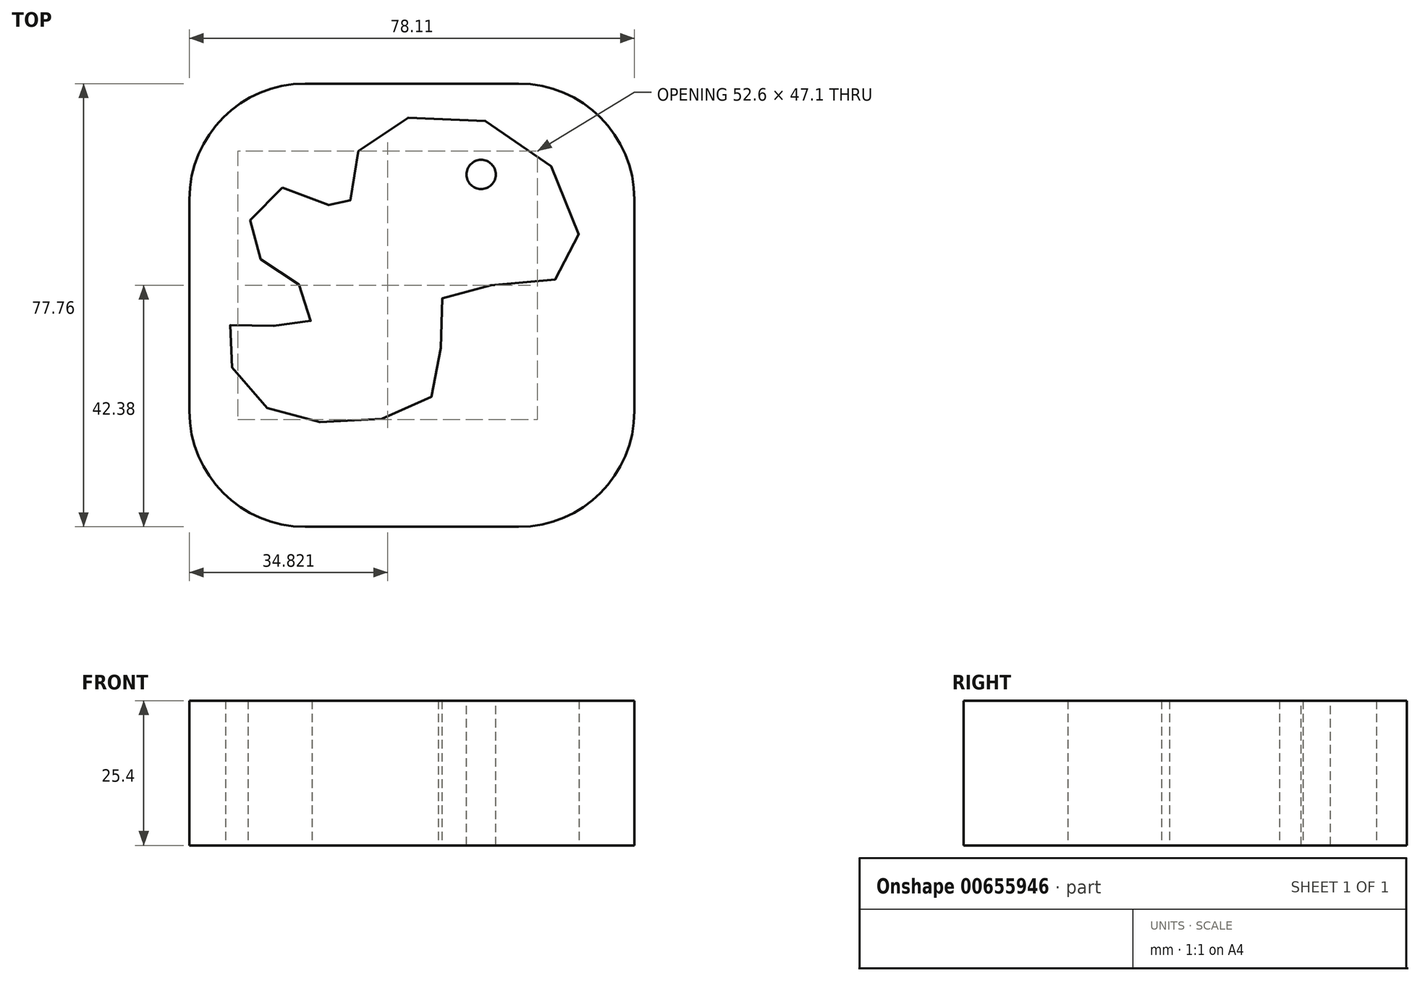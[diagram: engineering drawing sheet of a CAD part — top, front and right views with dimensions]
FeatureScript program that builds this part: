
annotation { "Feature Type Name" : "Feature", "Feature Type Description" : "" }
export const myFeature = defineFeature(function(context is Context, id is Id, definition is map)
    precondition{}
    {
        {
            var Q0;
            Q0=qCreatedBy(makeId("Top.planeOp"),FACE);
            var sketch = newSketch(context, id + "F0", { "sketchPlane" : qUnion([Q0])});
            skLineSegment(sketch, "E0.bottom", {"start": v(-136.12, 47) * mm, "end": v(-58, 47) * mm});
            skLineSegment(sketch, "E0.top", {"start": v(-136.12, -30.76) * mm, "end": v(-58, -30.76) * mm});
            skLineSegment(sketch, "E0.left", {"start": v(-136.12, 47) * mm, "end": v(-136.12, -30.76) * mm});
            skLineSegment(sketch, "E0.right", {"start": v(-58, 47) * mm, "end": v(-58, -30.76) * mm});
            skSolve(sketch);
        }
        {
            var Q0;
            Q0=makeQuery(id+"F0.imprint","IMPRINT",FACE,{"disambiguationData":[TD([[makeQuery(id+"F0.imprint","IMPRINT",EDGE,{"derivedFrom":sQuery(id+"F0.wireOp",EDGE,"E0.bottom")}),-1.0]])]});
            extrude(context, id + "F1", {"entities" : qUnion([Q0]), "depth" : 25.4 * mm, "offsetDistance" : 25.4 * mm});
        }
        {
            var Q0;
            Q0=makeQuery(id+"F1.opExtrude","CAP_FACE",FACE,{"disambiguationData":[OSD([sQuery(id+"F0.wireOp",EDGE,"E0.bottom"),sQuery(id+"F0.wireOp",EDGE,"E0.top"),sQuery(id+"F0.wireOp",EDGE,"E0.left"),sQuery(id+"F0.wireOp",EDGE,"E0.right")])],"isStart":false});
            var sketch = newSketch(context, id + "F2", { "sketchPlane" : qUnion([Q0])});
            skFitSpline(sketch, "E1", {"points": [v(-119.78, 28.73) * mm, v(-125.58, 18.83) * mm, v(-116.26, 11.07) * mm, v(-115.93, 4.23) * mm, v(-128.51, 4.94) * mm, v(-126.17, -6.83) * mm, v(-108.66, -12.45) * mm, v(-92.21, -5.58) * mm, v(-91.18, 10) * mm, v(-70.08, 13.7) * mm, v(-77.51, 37.26) * mm, v(-106, 35.99) * mm, v(-108.7, 24.71) * mm, v(-119.78, 28.73) * mm]});
            skCircle(sketch, "E2", {"center": v(-84.92, 31.06) * mm, "radius": 2.57 * mm});
            skSolve(sketch);
        }
        {
            var Q0;
            Q0 = qSketchRegion(id + "F2", true);
            extrude(context, id + "F3", {"entities" : qUnion([Q0]), "operationType" : NewBodyOperationType.REMOVE, "endBound" : BoundingType.THROUGH_ALL, "oppositeDirection" : true, "depth" : 25.4 * mm, "offsetDistance" : 25.4 * mm});
        }
        {
            var Q0;
            Q0=makeQuery(id+"F1.opExtrude","SWEPT_EDGE",EDGE,{"disambiguationData":[OSD([sQuery(id+"F0.wireOp",EDGE,"E0.top"),sQuery(id+"F0.wireOp",EDGE,"E0.right")])]});
            var Q1;
            Q1=makeQuery(id+"F1.opExtrude","SWEPT_EDGE",EDGE,{"disambiguationData":[OSD([sQuery(id+"F0.wireOp",EDGE,"E0.top"),sQuery(id+"F0.wireOp",EDGE,"E0.left")])]});
            var Q2;
            Q2=makeQuery(id+"F1.opExtrude","SWEPT_EDGE",EDGE,{"disambiguationData":[OSD([sQuery(id+"F0.wireOp",EDGE,"E0.bottom"),sQuery(id+"F0.wireOp",EDGE,"E0.right")])]});
            var Q3;
            Q3=makeQuery(id+"F1.opExtrude","SWEPT_EDGE",EDGE,{"disambiguationData":[OSD([sQuery(id+"F0.wireOp",EDGE,"E0.bottom"),sQuery(id+"F0.wireOp",EDGE,"E0.left")])]});
            fillet(context, id + "F4", {"entities" : qUnion([Q0, Q1, Q2, Q3]), "radius" : 20.32 * mm, "tangentPropagation" : true, "allowEdgeOverflow" : false});
        }
    });
